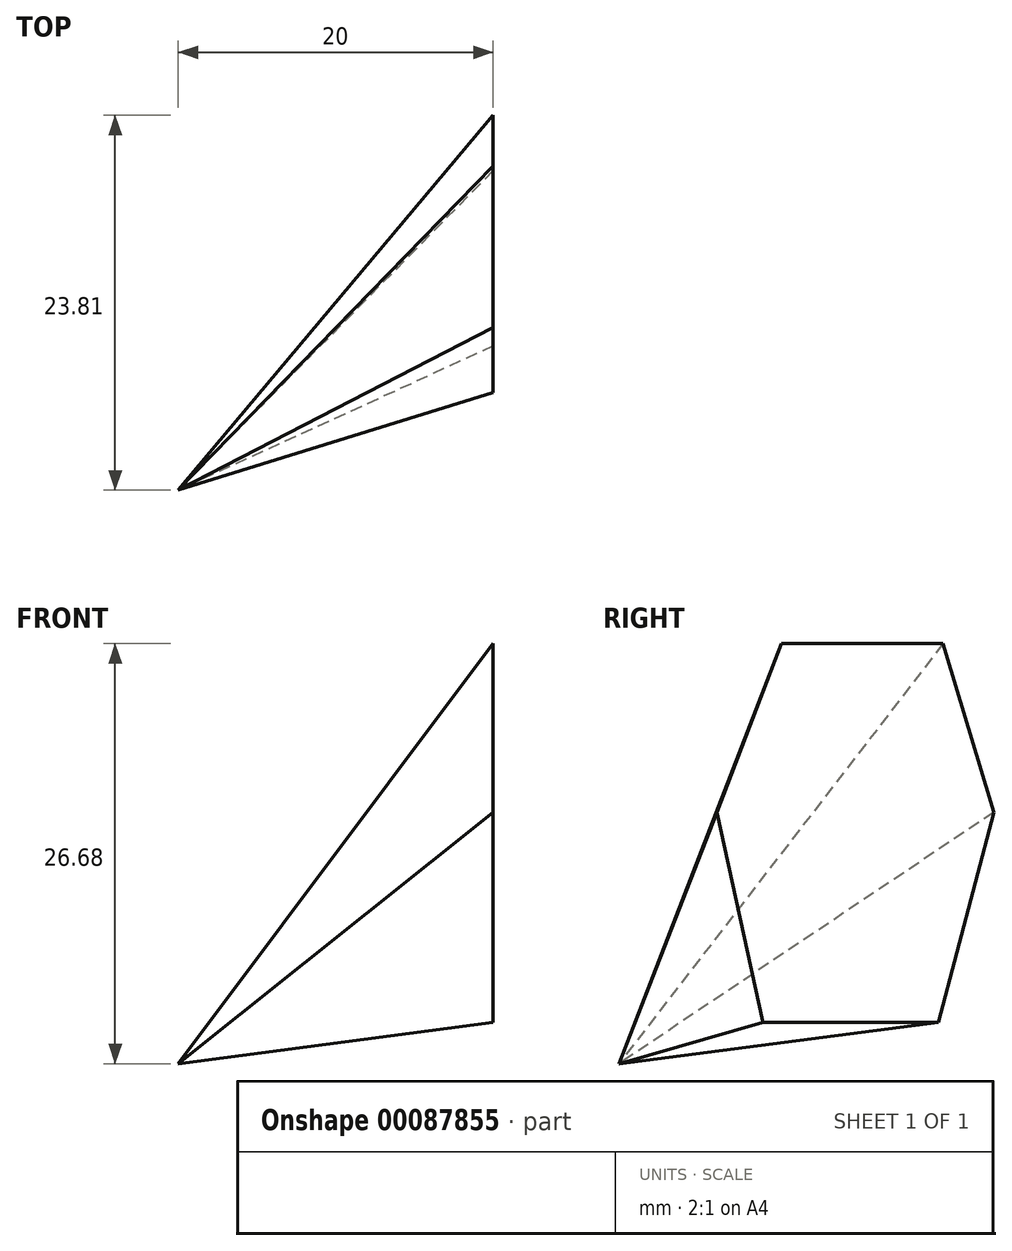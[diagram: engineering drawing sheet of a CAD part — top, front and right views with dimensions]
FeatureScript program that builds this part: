
annotation { "Feature Type Name" : "Feature", "Feature Type Description" : "" }
export const myFeature = defineFeature(function(context is Context, id is Id, definition is map)
    precondition{}
    {
        {
            var Q0;
            Q0=qCreatedBy(makeId("Right.planeOp"),FACE);
            var sketch = newSketch(context, id + "F0", { "sketchPlane" : qUnion([Q0])});
            skLineSegment(sketch, "E0.bottom", {"start": v(20, -25) * mm, "end": v(-20, -25) * mm});
            skLineSegment(sketch, "E0.top", {"start": v(20, 25) * mm, "end": v(-20, 25) * mm});
            skLineSegment(sketch, "E0.left", {"start": v(20, -25) * mm, "end": v(20, 25) * mm});
            skLineSegment(sketch, "E0.right", {"start": v(-20, -25) * mm, "end": v(-20, 25) * mm});
            skPoint(sketch, "E0.middle", {"position": v(0, 0) * mm});
            skLineSegment(sketch, "E1", {"start": v(-20, 0) * mm, "end": v(20, 0) * mm, "construction": true});
            skLineSegment(sketch, "E2", {"start": v(0, 25) * mm, "end": v(0, -25) * mm, "construction": true});
            skSolve(sketch);
        }
        {
            var Q0;
            Q0=qCreatedBy(makeId("Right.planeOp"),FACE);
            cPlane(context, id + "F1", {"entities" : qUnion([Q0]), "cplaneType" : CPlaneType.OFFSET, "offset" : 20 * mm, "width" : 150 * mm, "height" : 150 * mm});
        }
        {
            var Q0;
            Q0=qCreatedBy(id+"F1.planeOp",FACE);
            var sketch = newSketch(context, id + "F2", { "sketchPlane" : qUnion([Q0])});
            skLineSegment(sketch, "E3", {"start": v(0, 25.37) * mm, "end": v(0, -24.78) * mm, "construction": true});
            skLineSegment(sketch, "E4", {"start": v(-20.24, 0) * mm, "end": v(19.94, 0) * mm, "construction": true});
            skLineSegment(sketch, "E5", {"start": v(-8.21, 0) * mm, "end": v(-4.1, 10.7) * mm});
            skLineSegment(sketch, "E6", {"start": v(-4.1, 10.7) * mm, "end": v(6.16, 10.7) * mm});
            skLineSegment(sketch, "E7", {"start": v(6.16, 10.7) * mm, "end": v(9.39, 0) * mm});
            skLineSegment(sketch, "E8", {"start": v(9.39, 0) * mm, "end": v(5.87, -13.34) * mm});
            skLineSegment(sketch, "E9", {"start": v(5.87, -13.34) * mm, "end": v(-5.28, -13.34) * mm});
            skLineSegment(sketch, "E10", {"start": v(-5.28, -13.34) * mm, "end": v(-8.21, 0) * mm});
            skSolve(sketch);
        }
        {
            var Q0;
            Q0=sQuery(id+"F0.wireOp",VERTEX,"E1.start");
            var Q1;
            Q1=sQuery(id+"F2.wireOp",EDGE,"E5");
            cPlane(context, id + "F3", {"entities" : qUnion([Q0, Q1]), "cplaneType" : CPlaneType.LINE_ANGLE, "offset" : 150 * mm, "angle" : 0 * degree, "width" : 150 * mm, "height" : 150 * mm});
        }
        {
            var Q0;
            Q0=qCreatedBy(id+"F3.planeOp",FACE);
            var sketch = newSketch(context, id + "F4", { "sketchPlane" : qUnion([Q0])});
            skLineSegment(sketch, "E11", {"start": v(-9, -7.16) * mm, "end": v(13.83, 8.52) * mm});
            skLineSegment(sketch, "E12", {"start": v(13.83, 8.52) * mm, "end": v(13.83, -2.94) * mm});
            skLineSegment(sketch, "E13", {"start": v(13.83, -2.94) * mm, "end": v(-9, -7.16) * mm});
            skSolve(sketch);
        }
        {
            var Q0;
            Q0=sQuery(id+"F4.wireOp",VERTEX,"E13.end");
            var Q1;
            Q1=sQuery(id+"F4.wireOp",EDGE,"E12");
            var Q2;
            Q2=sQuery(id+"F4.wireOp",VERTEX,"E13.end");
            loft(context, id + "F5", {"bodyType" : ToolBodyType.SURFACE, "sheetProfilesArray" : [{ "sheetProfileEntities" : qUnion([Q0]) }], "wireProfilesArray" : [{ "wireProfileEntities" : qUnion([Q1]) }, { "wireProfileEntities" : qUnion([Q2]) }]});
        }
        {
            var Q0;
            Q0=sQuery(id+"F2.wireOp",EDGE,"E10");
            var Q1;
            Q1=sQuery(id+"F0.wireOp",VERTEX,"E1.start");
            cPlane(context, id + "F6", {"entities" : qUnion([Q0, Q1]), "cplaneType" : CPlaneType.LINE_ANGLE, "offset" : 150 * mm, "angle" : 0 * degree, "width" : 150 * mm, "height" : 150 * mm});
        }
        {
            var Q0;
            Q0=qCreatedBy(id+"F6.planeOp",FACE);
            var sketch = newSketch(context, id + "F7", { "sketchPlane" : qUnion([Q0])});
            skLineSegment(sketch, "E14", {"start": v(-9.75, 4.3) * mm, "end": v(13.33, 1.76) * mm});
            skLineSegment(sketch, "E15", {"start": v(13.33, 1.76) * mm, "end": v(13.33, -11.9) * mm});
            skLineSegment(sketch, "E16", {"start": v(13.33, -11.9) * mm, "end": v(-9.75, 4.3) * mm});
            skSolve(sketch);
        }
        {
            var Q0;
            Q0=sQuery(id+"F7.wireOp",VERTEX,"E16.end");
            var Q1;
            Q1=sQuery(id+"F7.wireOp",EDGE,"E15");
            loft(context, id + "F8", {"bodyType" : ToolBodyType.SURFACE, "wireProfilesArray" : [{ "wireProfileEntities" : qUnion([Q0]) }, { "wireProfileEntities" : qUnion([Q1]) }]});
        }
        {
            var Q0;
            Q0=qCreatedBy(makeId("Right.planeOp"),FACE);
            var sketch = newSketch(context, id + "F9", { "sketchPlane" : qUnion([Q0])});
            skLineSegment(sketch, "E17", {"start": v(-20.24, 0) * mm, "end": v(-14.42, -15.97) * mm});
            skSolve(sketch);
        }
        {
            var Q0;
            Q0=sQuery(id+"F9.wireOp",EDGE,"E17");
            var Q1;
            Q1=sQuery(id+"F2.wireOp",VERTEX,"E10.start");
            loft(context, id + "F10", {"bodyType" : ToolBodyType.SURFACE, "wireProfilesArray" : [{ "wireProfileEntities" : qUnion([Q0]) }, { "wireProfileEntities" : qUnion([Q1]) }]});
        }
        {
            var Q0;
            Q0=qCreatedBy(makeId("Right.planeOp"),FACE);
            var sketch = newSketch(context, id + "F11", { "sketchPlane" : qUnion([Q0])});
            skLineSegment(sketch, "E18", {"start": v(-9, 13) * mm, "end": v(9.25, 13) * mm});
            skSolve(sketch);
        }
        {
            var Q0;
            Q0=sQuery(id+"F11.wireOp",EDGE,"E18");
            var Q1;
            Q1=sQuery(id+"F2.wireOp",EDGE,"E6");
            loft(context, id + "F12", {"bodyType" : ToolBodyType.SURFACE, "wireProfilesArray" : [{ "wireProfileEntities" : qUnion([Q0]) }, { "wireProfileEntities" : qUnion([Q1]) }]});
        }
        {
            var Q0;
            Q0=makeQuery(id+"F12.opLoft","SWEPT_EDGE",EDGE,{"disambiguationData":[OSD([sQuery(id+"F2.wireOp",VERTEX,"E6.start"),sQuery(id+"F11.wireOp",VERTEX,"E18.start")])]});
            var Q1;
            Q1=makeQuery(id+"F5.opLoft","SWEPT_EDGE",EDGE,{"disambiguationData":[OSD([sQuery(id+"F4.wireOp",VERTEX,"E12.start"),sQuery(id+"F4.wireOp",VERTEX,"E13.end")])]});
            loft(context, id + "F13", {"bodyType" : ToolBodyType.SURFACE, "wireProfilesArray" : [{ "wireProfileEntities" : qUnion([Q0]) }, { "wireProfileEntities" : qUnion([Q1]) }]});
        }
        {
            var Q0;
            Q0=qCreatedBy(makeId("Right.planeOp"),FACE);
            var sketch = newSketch(context, id + "F14", { "sketchPlane" : qUnion([Q0])});
            skLineSegment(sketch, "E19", {"start": v(9.25, 13) * mm, "end": v(19.94, 0) * mm});
            skLineSegment(sketch, "E20", {"start": v(13.7, -15.88) * mm, "end": v(19.94, 0) * mm});
            skSolve(sketch);
        }
        {
            var Q0;
            Q0=sQuery(id+"F14.wireOp",EDGE,"E19");
            var Q1;
            Q1=sQuery(id+"F2.wireOp",EDGE,"E7");
            loft(context, id + "F15", {"bodyType" : ToolBodyType.SURFACE, "wireProfilesArray" : [{ "wireProfileEntities" : qUnion([Q0]) }, { "wireProfileEntities" : qUnion([Q1]) }]});
        }
        {
            var Q0;
            Q0 = qSketchRegion(id + "F14", true);
            var Q1;
            Q1=sQuery(id+"F2.wireOp",EDGE,"E8");
            var Q2;
            Q2=sQuery(id+"F14.wireOp",EDGE,"E20");
            loft(context, id + "F16", {"bodyType" : ToolBodyType.SURFACE, "sheetProfilesArray" : [{ "sheetProfileEntities" : qUnion([Q0]) }], "wireProfilesArray" : [{ "wireProfileEntities" : qUnion([Q1]) }, { "wireProfileEntities" : qUnion([Q2]) }]});
        }
        {
            var Q0;
            Q0=makeQuery(id+"F16.opLoft","SWEPT_EDGE",EDGE,{"disambiguationData":[OSD([sQuery(id+"F2.wireOp",VERTEX,"E8.end"),sQuery(id+"F14.wireOp",VERTEX,"E20.start")])]});
            var Q1;
            Q1=makeQuery(id+"F10.opLoft","SWEPT_EDGE",EDGE,{"disambiguationData":[OSD([sQuery(id+"F2.wireOp",VERTEX,"E10.start"),sQuery(id+"F9.wireOp",VERTEX,"E17.end")])]});
            loft(context, id + "F17", {"bodyType" : ToolBodyType.SURFACE, "wireProfilesArray" : [{ "wireProfileEntities" : qUnion([Q0]) }, { "wireProfileEntities" : qUnion([Q1]) }]});
        }
        {
            var Q0;
            Q0=sQuery(id+"F2.wireOp",EDGE,"E5");
            var Q1;
            Q1=sQuery(id+"F2.wireOp",EDGE,"E7");
            loft(context, id + "F18", {"bodyType" : ToolBodyType.SURFACE, "wireProfilesArray" : [{ "wireProfileEntities" : qUnion([Q0]) }, { "wireProfileEntities" : qUnion([Q1]) }]});
        }
        {
            var Q0;
            Q0=sQuery(id+"F2.wireOp",EDGE,"E8");
            var Q1;
            Q1=sQuery(id+"F2.wireOp",EDGE,"E10");
            loft(context, id + "F19", {"bodyType" : ToolBodyType.SURFACE, "wireProfilesArray" : [{ "wireProfileEntities" : qUnion([Q0]) }, { "wireProfileEntities" : qUnion([Q1]) }]});
        }
        {
            var Q0;
            Q0=sQuery(id+"F14.wireOp",EDGE,"E19");
            var Q1;
            Q1=makeQuery(id+"F13.opLoft","SWEPT_EDGE",EDGE,{"disambiguationData":[OSD([sQuery(id+"F4.wireOp",VERTEX,"E12.end"),sQuery(id+"F4.wireOp",VERTEX,"E13.end"),sQuery(id+"F11.wireOp",VERTEX,"E18.start")])]});
            loft(context, id + "F20", {"bodyType" : ToolBodyType.SURFACE, "wireProfilesArray" : [{ "wireProfileEntities" : qUnion([Q0]) }, { "wireProfileEntities" : qUnion([Q1]) }]});
        }
        {
            var Q0;
            Q0=sQuery(id+"F14.wireOp",EDGE,"E20");
            var Q1;
            Q1=makeQuery(id+"F10.opLoft","MID_CAP_EDGE",EDGE,{"disambiguationData":[OSD([sQuery(id+"F9.wireOp",VERTEX,"E17.start"),sQuery(id+"F9.wireOp",VERTEX,"E17.end"),sQuery(id+"F9.wireOp",EDGE,"E17")])],"capPos":0.0});
            loft(context, id + "F21", {"bodyType" : ToolBodyType.SURFACE, "wireProfilesArray" : [{ "wireProfileEntities" : qUnion([Q0]) }, { "wireProfileEntities" : qUnion([Q1]) }]});
        }
        {
            var Q0;
            Q0=makeQuery(id+"F2.imprint","IMPRINT",FACE,{"disambiguationData":[TD([[makeQuery(id+"F2.imprint","IMPRINT",EDGE,{"derivedFrom":sQuery(id+"F2.wireOp",EDGE,"E5")}),-1.0]])]});
            var Q1;
            Q1=makeQuery(id+"F10.opLoft","MID_CAP_VERTEX",VERTEX,{"disambiguationData":[OSD([sQuery(id+"F9.wireOp",VERTEX,"E17.end")])],"capPos":0.0});
            loft(context, id + "F22", {"sheetProfilesArray" : [{ "sheetProfileEntities" : qUnion([Q0]) }, { "sheetProfileEntities" : qUnion([Q1]) }]});
        }
    });
